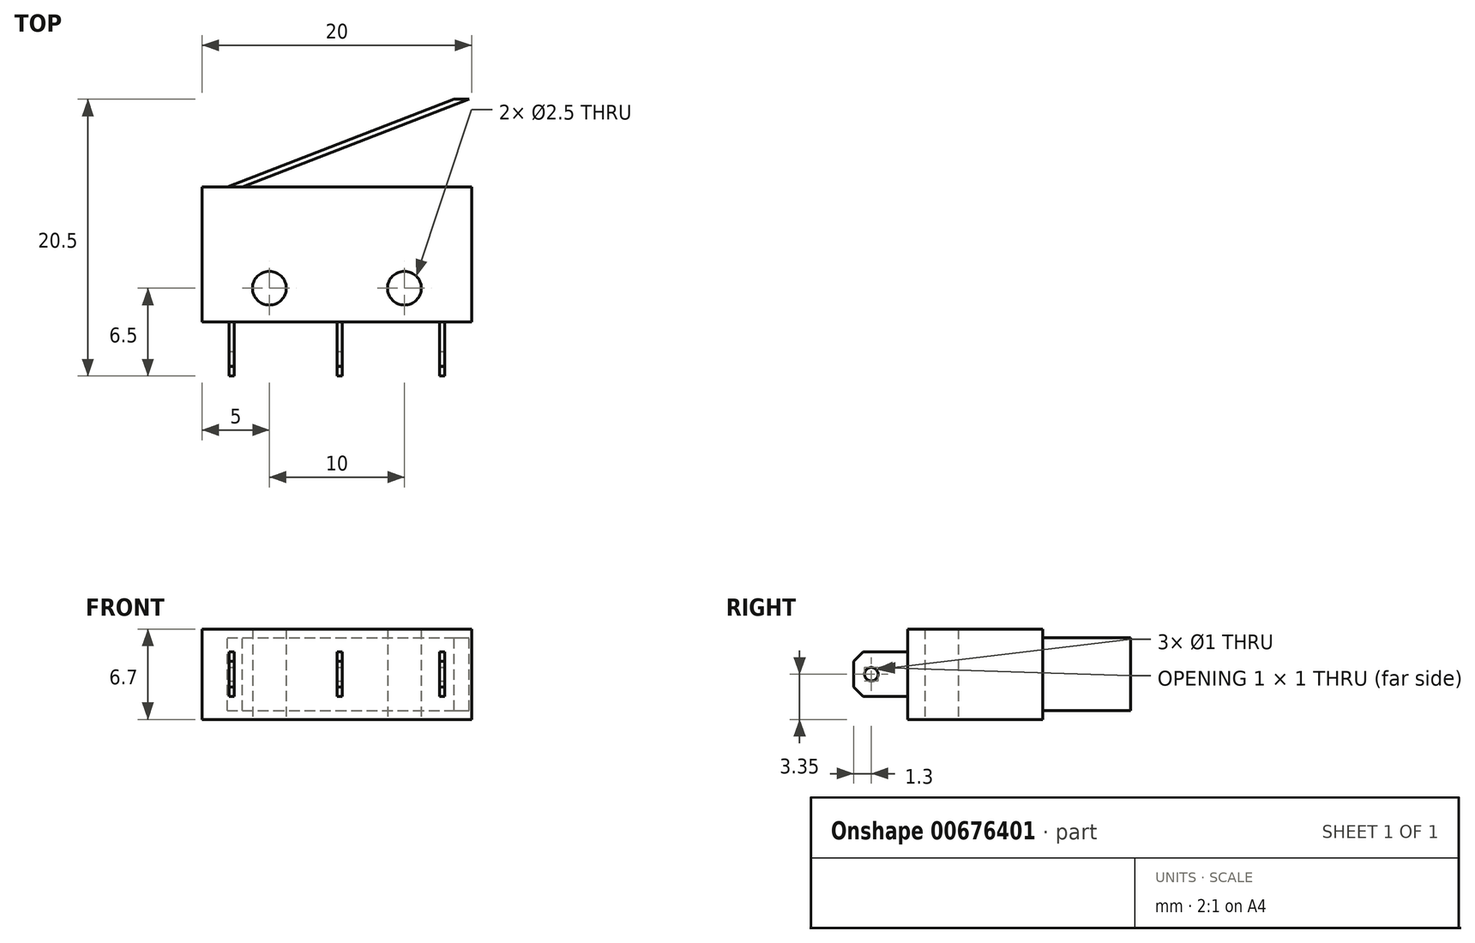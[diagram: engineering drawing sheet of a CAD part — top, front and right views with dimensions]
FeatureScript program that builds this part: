
annotation { "Feature Type Name" : "Feature", "Feature Type Description" : "" }
export const myFeature = defineFeature(function(context is Context, id is Id, definition is map)
    precondition{}
    {
        {
            var Q0;
            Q0=qCreatedBy(makeId("Top.planeOp"),FACE);
            var sketch = newSketch(context, id + "F0", { "sketchPlane" : qUnion([Q0])});
            skLineSegment(sketch, "E0.bottom", {"start": v(-10, 5) * mm, "end": v(10, 5) * mm});
            skLineSegment(sketch, "E0.top", {"start": v(-10, -5) * mm, "end": v(10, -5) * mm});
            skLineSegment(sketch, "E0.left", {"start": v(-10, 5) * mm, "end": v(-10, -5) * mm});
            skLineSegment(sketch, "E0.right", {"start": v(10, 5) * mm, "end": v(10, -5) * mm});
            skPoint(sketch, "E0.middle", {"position": v(0, 0) * mm});
            skCircle(sketch, "E1", {"center": v(-5, -2.5) * mm, "radius": 1.25 * mm});
            skCircle(sketch, "E2", {"center": v(5, -2.5) * mm, "radius": 1.25 * mm});
            skLineSegment(sketch, "E3", {"start": v(-7, 5) * mm, "end": v(9.79, 11.5) * mm});
            skLineSegment(sketch, "E4", {"start": v(-8, -5) * mm, "end": v(-8, -9) * mm});
            skLineSegment(sketch, "E5", {"start": v(0, -5) * mm, "end": v(0, -9) * mm});
            skLineSegment(sketch, "E6", {"start": v(8, -5) * mm, "end": v(8, -9) * mm});
            skLineSegment(sketch, "E7", {"start": v(0, 0) * mm, "end": v(0, -5) * mm, "construction": true});
            skArc(sketch, "E8", {"start": v(11, 5) * mm, "mid": v(10.7, 8.3) * mm, "end": v(9.79, 11.5) * mm, "construction": true});
            skSolve(sketch);
        }
        {
            var Q0;
            {var subQ3=sQuery(id+"F0.wireOp",EDGE,"E0.left");Q0=makeQuery(id+"F0.imprint","IMPRINT",FACE,{"disambiguationData":[TD([[makeQuery(id+"F0.imprint","IMPRINT",EDGE,{"derivedFrom":subQ3}),1.0]])]});}
            extrude(context, id + "F1", {"entities" : qUnion([Q0]), "flatOperationType" : FlatOperationType.REMOVE, "depth" : 6.7 * mm, "offsetDistance" : 25 * mm, "domain" : OperationDomain.MODEL});
        }
        {
            var Q0;
            Q0=makeQuery(id+"F1.opExtrude","SWEPT_FACE",FACE,{"disambiguationData":[OSD([sQuery(id+"F0.wireOp",EDGE,"E0.top")])]});
            var sketch = newSketch(context, id + "F2", { "sketchPlane" : qUnion([Q0])});
            skLineSegment(sketch, "E9.bottom", {"start": v(-8, 1.7) * mm, "end": v(-7.6, 1.7) * mm});
            skLineSegment(sketch, "E9.top", {"start": v(-8, 5) * mm, "end": v(-7.6, 5) * mm});
            skLineSegment(sketch, "E9.left", {"start": v(-8, 1.7) * mm, "end": v(-8, 5) * mm});
            skLineSegment(sketch, "E9.right", {"start": v(-7.6, 1.7) * mm, "end": v(-7.6, 5) * mm});
            skLineSegment(sketch, "E10.bottom", {"start": v(0, 1.7) * mm, "end": v(0.4, 1.7) * mm});
            skLineSegment(sketch, "E10.top", {"start": v(0, 5) * mm, "end": v(0.4, 5) * mm});
            skLineSegment(sketch, "E10.left", {"start": v(0, 1.7) * mm, "end": v(0, 5) * mm});
            skLineSegment(sketch, "E10.right", {"start": v(0.4, 1.7) * mm, "end": v(0.4, 5) * mm});
            skLineSegment(sketch, "E11.bottom", {"start": v(8, 1.7) * mm, "end": v(7.6, 1.7) * mm});
            skLineSegment(sketch, "E11.top", {"start": v(8, 5) * mm, "end": v(7.6, 5) * mm});
            skLineSegment(sketch, "E11.left", {"start": v(8, 1.7) * mm, "end": v(8, 5) * mm});
            skLineSegment(sketch, "E11.right", {"start": v(7.6, 1.7) * mm, "end": v(7.6, 5) * mm});
            skLineSegment(sketch, "E12", {"start": v(-7.6, 3.35) * mm, "end": v(10, 3.35) * mm, "construction": true});
            skSolve(sketch);
        }
        {
            var Q0;
            Q0=makeQuery(id+"F1.opExtrude","SWEPT_FACE",FACE,{"disambiguationData":[OSD([sQuery(id+"F0.wireOp",EDGE,"E0.bottom")])]});
            var sketch = newSketch(context, id + "F3", { "sketchPlane" : qUnion([Q0])});
            skLineSegment(sketch, "E13.bottom", {"start": v(8.1, 0.65) * mm, "end": v(7, 0.65) * mm});
            skLineSegment(sketch, "E13.top", {"start": v(8.1, 6.05) * mm, "end": v(7, 6.05) * mm});
            skLineSegment(sketch, "E13.left", {"start": v(7, 0.65) * mm, "end": v(7, 6.05) * mm});
            skLineSegment(sketch, "E13.right", {"start": v(8.1, 0.65) * mm, "end": v(8.1, 6.05) * mm});
            skLineSegment(sketch, "E14", {"start": v(8.1, 3.35) * mm, "end": v(10, 3.35) * mm, "construction": true});
            skSolve(sketch);
        }
        {
            var Q0;
            Q0=makeQuery(id+"F2.imprint","IMPRINT",FACE,{"disambiguationData":[TD([[makeQuery(id+"F2.imprint","IMPRINT",EDGE,{"derivedFrom":sQuery(id+"F2.wireOp",EDGE,"E9.bottom")}),1.0]])]});
            var Q1;
            Q1=makeQuery(id+"F2.imprint","IMPRINT",FACE,{"disambiguationData":[TD([[makeQuery(id+"F2.imprint","IMPRINT",EDGE,{"derivedFrom":sQuery(id+"F2.wireOp",EDGE,"E10.bottom")}),1.0]])]});
            var Q2;
            Q2=makeQuery(id+"F2.imprint","IMPRINT",FACE,{"disambiguationData":[TD([[makeQuery(id+"F2.imprint","IMPRINT",EDGE,{"derivedFrom":sQuery(id+"F2.wireOp",EDGE,"E11.bottom")}),-1.0]])]});
            var Q3;
            Q3=sQuery(id+"F0.wireOp",EDGE,"E4");
            sweep(context, id + "F4", {"operationType" : NewBodyOperationType.ADD, "profiles" : qUnion([Q0, Q1, Q2]), "path" : qUnion([Q3])});
        }
        {
            var Q0;
            Q0=makeQuery(id+"F3.imprint","IMPRINT",FACE,{"disambiguationData":[TD([[makeQuery(id+"F3.imprint","IMPRINT",EDGE,{"derivedFrom":sQuery(id+"F3.wireOp",EDGE,"E13.bottom")}),-1.0]])]});
            var Q1;
            Q1=sQuery(id+"F0.wireOp",EDGE,"E3");
            sweep(context, id + "F5", {"operationType" : NewBodyOperationType.ADD, "profiles" : qUnion([Q0]), "path" : qUnion([Q1])});
        }
        {
            var Q0;
            Q0=makeQuery(id+"F4.opSweep","SWEPT_FACE",FACE,{"disambiguationData":[OSD([sQuery(id+"F0.wireOp",EDGE,"E4"),sQuery(id+"F2.wireOp",EDGE,"E11.left")])]});
            var sketch = newSketch(context, id + "F6", { "sketchPlane" : qUnion([Q0])});
            skCircle(sketch, "E15", {"center": v(-7.7, 3.35) * mm, "radius": 0.5 * mm});
            skLineSegment(sketch, "E16", {"start": v(-7.7, 3.35) * mm, "end": v(-9, 3.35) * mm, "construction": true});
            skSolve(sketch);
        }
        {
            var Q0;
            Q0=makeQuery(id+"F6.imprint","IMPRINT",FACE,{"disambiguationData":[TD([[makeQuery(id+"F6.imprint","IMPRINT",EDGE,{"derivedFrom":sQuery(id+"F6.wireOp",EDGE,"E15")}),1.0]])]});
            extrude(context, id + "F7", {"entities" : qUnion([Q0]), "operationType" : NewBodyOperationType.REMOVE, "oppositeDirection" : true, "depth" : 25 * mm, "offsetDistance" : 25 * mm});
        }
        {
            var Q0;
            Q0=makeQuery(id+"F4.opSweep","CAP_EDGE",EDGE,{"disambiguationData":[OSD([sQuery(id+"F0.wireOp",VERTEX,"E4.end"),sQuery(id+"F2.wireOp",EDGE,"E9.top")])],"isStart":false});
            var Q1;
            Q1=makeQuery(id+"F4.opSweep","CAP_EDGE",EDGE,{"disambiguationData":[OSD([sQuery(id+"F0.wireOp",VERTEX,"E4.end"),sQuery(id+"F2.wireOp",EDGE,"E10.top")])],"isStart":false});
            var Q2;
            Q2=makeQuery(id+"F4.opSweep","CAP_EDGE",EDGE,{"disambiguationData":[OSD([sQuery(id+"F0.wireOp",VERTEX,"E4.end"),sQuery(id+"F2.wireOp",EDGE,"E11.top")])],"isStart":false});
            var Q3;
            Q3=makeQuery(id+"F4.opSweep","CAP_EDGE",EDGE,{"disambiguationData":[OSD([sQuery(id+"F0.wireOp",VERTEX,"E4.end"),sQuery(id+"F2.wireOp",EDGE,"E9.bottom")])],"isStart":false});
            var Q4;
            Q4=makeQuery(id+"F4.opSweep","CAP_EDGE",EDGE,{"disambiguationData":[OSD([sQuery(id+"F0.wireOp",VERTEX,"E4.end"),sQuery(id+"F2.wireOp",EDGE,"E10.bottom")])],"isStart":false});
            var Q5;
            Q5=makeQuery(id+"F4.opSweep","CAP_EDGE",EDGE,{"disambiguationData":[OSD([sQuery(id+"F0.wireOp",VERTEX,"E4.end"),sQuery(id+"F2.wireOp",EDGE,"E11.bottom")])],"isStart":false});
            chamfer(context, id + "F8", {"entities" : qUnion([Q0, Q1, Q2, Q3, Q4, Q5]), "width" : 0.7 * mm, "tangentPropagation" : true});
        }
    });
